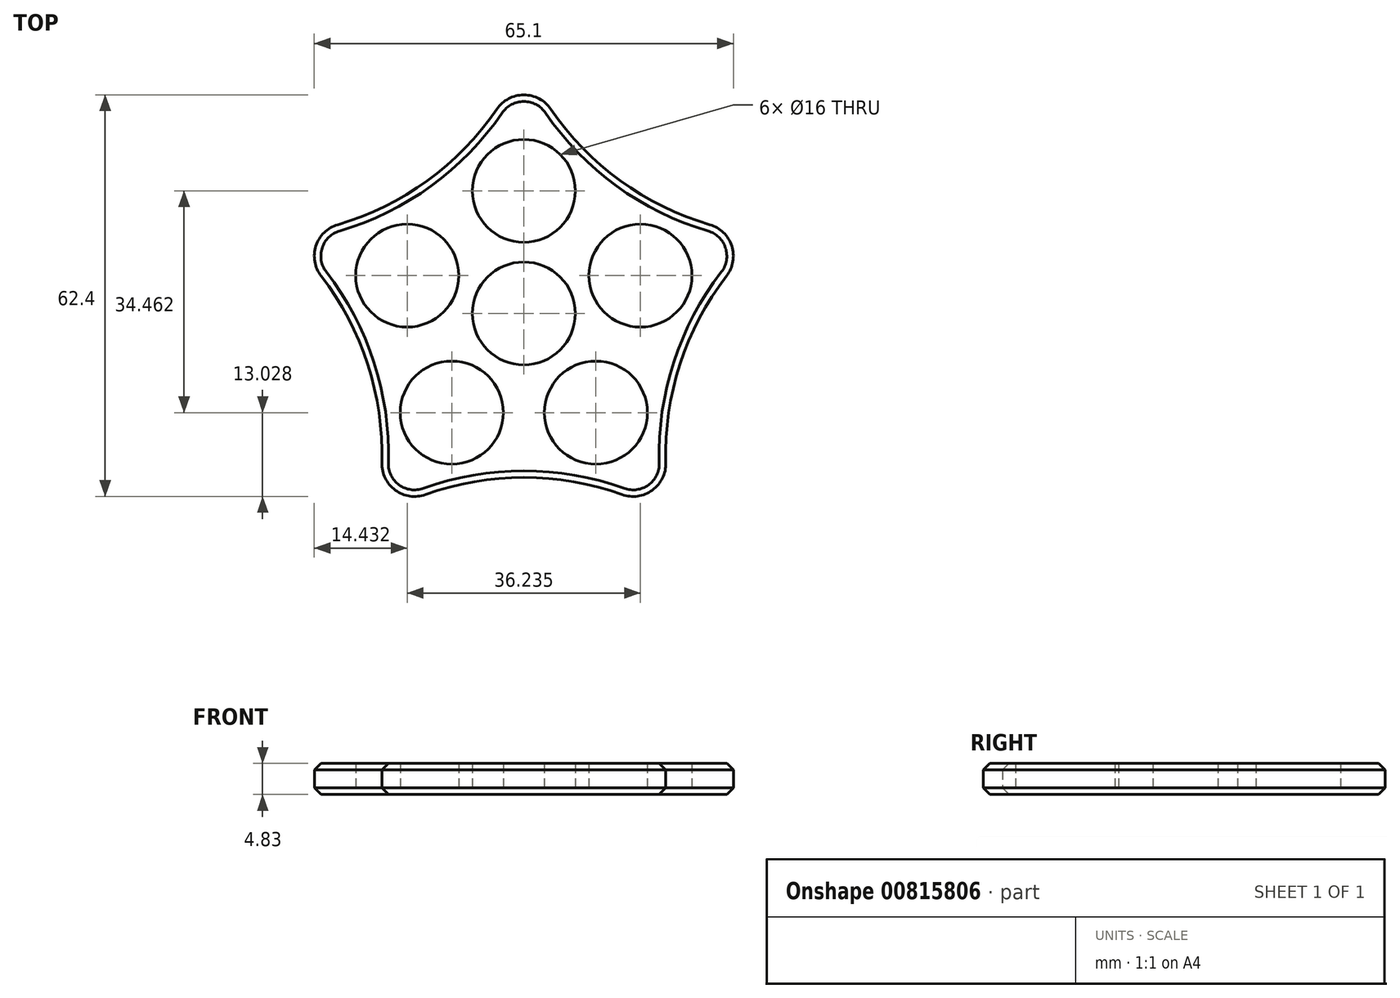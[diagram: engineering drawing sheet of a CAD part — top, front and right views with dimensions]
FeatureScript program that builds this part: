
annotation { "Feature Type Name" : "Feature", "Feature Type Description" : "" }
export const myFeature = defineFeature(function(context is Context, id is Id, definition is map)
    precondition{}
    {
        {
            var Q0;
            Q0=qCreatedBy(makeId("Top.planeOp"),FACE);
            var sketch = newSketch(context, id + "F0", { "sketchPlane" : qUnion([Q0])});
            skCircle(sketch, "E0.cCircle", {"center": v(0, 0) * mm, "radius": 39.37 * mm, "construction": true});
            skLineSegment(sketch, "E0.0", {"start": v(-37.44, 12.17) * mm, "end": v(0, 39.37) * mm, "construction": true});
            skLineSegment(sketch, "E0.1", {"start": v(0, 39.37) * mm, "end": v(37.44, 12.17) * mm, "construction": true});
            skLineSegment(sketch, "E0.2", {"start": v(37.44, 12.17) * mm, "end": v(23.14, -31.85) * mm, "construction": true});
            skLineSegment(sketch, "E0.3", {"start": v(23.14, -31.85) * mm, "end": v(-23.14, -31.85) * mm, "construction": true});
            skLineSegment(sketch, "E0.4", {"start": v(-23.14, -31.85) * mm, "end": v(-37.44, 12.17) * mm, "construction": true});
            skLineSegment(sketch, "E1", {"start": v(0, 0) * mm, "end": v(-30.3, -9.84) * mm, "construction": true});
            skPoint(sketch, "E2", {"position": v(-30.3, -9.84) * mm});
            skArc(sketch, "E3", {"start": v(-23.14, -31.85) * mm, "mid": v(-24.25, -7.88) * mm, "end": v(-37.44, 12.17) * mm});
            skArc(sketch, "E4.1.0", {"start": v(23.14, -31.85) * mm, "mid": v(0, -25.5) * mm, "end": v(-23.14, -31.85) * mm});
            skArc(sketch, "E4.2.0", {"start": v(37.44, 12.17) * mm, "mid": v(24.25, -7.88) * mm, "end": v(23.14, -31.85) * mm});
            skLineSegment(sketch, "E4.2.1", {"start": v(0, 0) * mm, "end": v(30.3, -9.84) * mm, "construction": true});
            skArc(sketch, "E4.3.0", {"start": v(0, 39.37) * mm, "mid": v(14.99, 20.63) * mm, "end": v(37.44, 12.17) * mm});
            skLineSegment(sketch, "E4.3.1", {"start": v(0, 0) * mm, "end": v(18.72, 25.77) * mm, "construction": true});
            skArc(sketch, "E4.4.0", {"start": v(-37.44, 12.17) * mm, "mid": v(-14.99, 20.63) * mm, "end": v(0, 39.37) * mm});
            skLineSegment(sketch, "E4.4.1", {"start": v(0, 0) * mm, "end": v(-18.72, 25.77) * mm, "construction": true});
            skLineSegment(sketch, "E5", {"start": v(0, 0) * mm, "end": v(0, -31.85) * mm, "construction": true});
            skCircle(sketch, "E6", {"center": v(0, 0) * mm, "radius": 8 * mm});
            skCircle(sketch, "E7", {"center": v(-18.12, 5.89) * mm, "radius": 8 * mm});
            skCircle(sketch, "E8.1.0", {"center": v(-11.2, -15.41) * mm, "radius": 8 * mm});
            skCircle(sketch, "E8.2.0", {"center": v(11.2, -15.41) * mm, "radius": 8 * mm});
            skCircle(sketch, "E8.3.0", {"center": v(18.12, 5.89) * mm, "radius": 8 * mm});
            skCircle(sketch, "E8.4.0", {"center": v(0, 19.05) * mm, "radius": 8 * mm});
            skLineSegment(sketch, "E9", {"start": v(0, 0) * mm, "end": v(-18.12, 5.89) * mm, "construction": true});
            skLineSegment(sketch, "E10", {"start": v(0, 0) * mm, "end": v(-11.2, -15.41) * mm, "construction": true});
            skLineSegment(sketch, "E11", {"start": v(11.2, -15.41) * mm, "end": v(0, 0) * mm, "construction": true});
            skSolve(sketch);
        }
        {
            var Q0;
            Q0=qSketchRegion(id+"F0",true);
            extrude(context, id + "F1", {"entities" : qUnion([Q0]), "depth" : 4.83 * mm, "offsetDistance" : 25.4 * mm});
        }
        {
            var Q0;
            Q0=makeQuery(id+"F1.opExtrude","SWEPT_EDGE",EDGE,{"disambiguationData":[OSD([sQuery(id+"F0.wireOp",EDGE,"E4.3.0"),sQuery(id+"F0.wireOp",EDGE,"E4.4.0")])]});
            var Q1;
            Q1=makeQuery(id+"F1.opExtrude","SWEPT_EDGE",EDGE,{"disambiguationData":[OSD([sQuery(id+"F0.wireOp",EDGE,"E4.2.0"),sQuery(id+"F0.wireOp",EDGE,"E4.3.0")])]});
            var Q2;
            Q2=makeQuery(id+"F1.opExtrude","SWEPT_EDGE",EDGE,{"disambiguationData":[OSD([sQuery(id+"F0.wireOp",EDGE,"E4.1.0"),sQuery(id+"F0.wireOp",EDGE,"E4.2.0")])]});
            var Q3;
            Q3=makeQuery(id+"F1.opExtrude","SWEPT_EDGE",EDGE,{"disambiguationData":[OSD([sQuery(id+"F0.wireOp",EDGE,"E3"),sQuery(id+"F0.wireOp",EDGE,"E4.1.0")])]});
            var Q4;
            Q4=makeQuery(id+"F1.opExtrude","SWEPT_EDGE",EDGE,{"disambiguationData":[OSD([sQuery(id+"F0.wireOp",EDGE,"E3"),sQuery(id+"F0.wireOp",EDGE,"E4.4.0")])]});
            fillet(context, id + "F2", {"entities" : qUnion([Q0, Q1, Q2, Q3, Q4]), "radius" : 5.08 * mm, "tangentPropagation" : true, "allowEdgeOverflow" : false});
        }
        {
            var Q0;
            {var subQ0=sQuery(id+"F0.wireOp",EDGE,"E4.4.0");var subQ1=sQuery(id+"F0.wireOp",EDGE,"E3");Q0=makeQuery(id+"F2.opFillet","BLEND_EDGE",EDGE,{"blendedFrom":[makeQuery(id+"F1.opExtrude","SWEPT_EDGE",EDGE,{"disambiguationData":[OSD([subQ1,subQ0])]}),makeQuery(id+"F1.opExtrude","CAP_FACE",FACE,{"disambiguationData":[OSD([subQ1,sQuery(id+"F0.wireOp",EDGE,"E4.1.0"),sQuery(id+"F0.wireOp",EDGE,"E4.2.0"),sQuery(id+"F0.wireOp",EDGE,"E4.3.0"),subQ0,sQuery(id+"F0.wireOp",EDGE,"E6"),sQuery(id+"F0.wireOp",EDGE,"E7"),sQuery(id+"F0.wireOp",EDGE,"E8.1.0"),sQuery(id+"F0.wireOp",EDGE,"E8.2.0"),sQuery(id+"F0.wireOp",EDGE,"E8.3.0"),sQuery(id+"F0.wireOp",EDGE,"E8.4.0")])],"isStart":true})],"blendedInto":[makeQuery(id+"F1.opExtrude","CAP_FACE",FACE,{"disambiguationData":[OSD([subQ1,sQuery(id+"F0.wireOp",EDGE,"E4.1.0"),sQuery(id+"F0.wireOp",EDGE,"E4.2.0"),sQuery(id+"F0.wireOp",EDGE,"E4.3.0"),subQ0,sQuery(id+"F0.wireOp",EDGE,"E6"),sQuery(id+"F0.wireOp",EDGE,"E7"),sQuery(id+"F0.wireOp",EDGE,"E8.1.0"),sQuery(id+"F0.wireOp",EDGE,"E8.2.0"),sQuery(id+"F0.wireOp",EDGE,"E8.3.0"),sQuery(id+"F0.wireOp",EDGE,"E8.4.0")])],"isStart":true})]});}
            var Q1;
            Q1=makeQuery(id+"F1.opExtrude","CAP_EDGE",EDGE,{"disambiguationData":[OSD([sQuery(id+"F0.wireOp",EDGE,"E3")])],"isStart":false});
            chamfer(context, id + "F3", {"entities" : qUnion([Q0, Q1]), "width" : 1.02 * mm, "tangentPropagation" : true});
        }
    });
